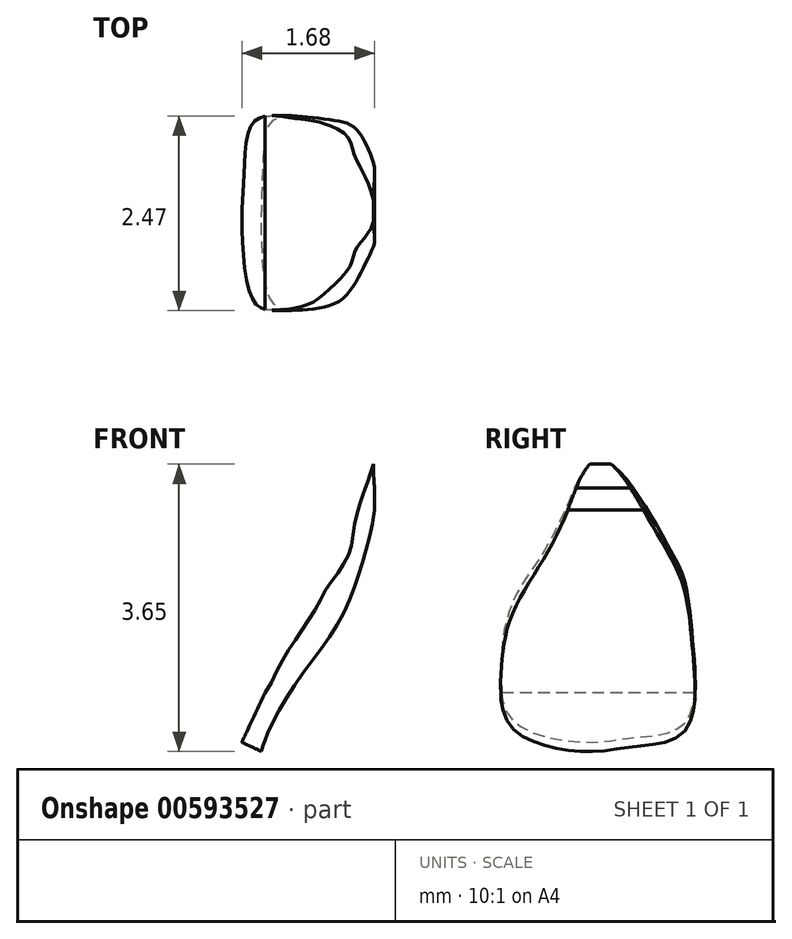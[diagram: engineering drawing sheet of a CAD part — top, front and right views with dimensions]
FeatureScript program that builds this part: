
annotation { "Feature Type Name" : "Feature", "Feature Type Description" : "" }
export const myFeature = defineFeature(function(context is Context, id is Id, definition is map)
    precondition{}
    {
        {
            var Q0;
            Q0=qCreatedBy(makeId("Right.planeOp"),FACE);
            var sketch = newSketch(context, id + "F0", { "sketchPlane" : qUnion([Q0])});
            skFitSpline(sketch, "E0", {"points": [v(-2.15, -4.24) * mm, v(-1.2, -4.53) * mm, v(-0.65, -4.46) * mm, v(0, -4.27) * mm, v(0.11, -3.1) * mm, v(0, -2.14) * mm, v(-0.34, -1.44) * mm, v(-1.07, -0.56) * mm, v(-1.5, -1.21) * mm, v(-1.8, -1.8) * mm, v(-2.2, -2.6) * mm, v(-2.32, -3.48) * mm, v(-2.15, -4.24) * mm]});
            skSolve(sketch);
        }
        {
            var Q0;
            Q0 = qSketchRegion(id + "F0", true);
            extrude(context, id + "F1", {"entities" : qUnion([Q0]), "endBound" : BoundingType.SYMMETRIC, "depth" : 0.6 * mm, "offsetDistance" : 25 * mm});
        }
        {
            var Q0;
            Q0=qCreatedBy(makeId("Right.planeOp"),FACE);
            var sketch = newSketch(context, id + "F2", { "sketchPlane" : qUnion([Q0])});
            skLineSegment(sketch, "E1", {"start": v(0, 11.64) * mm, "end": v(0, -10.45) * mm});
            skLineSegment(sketch, "E2", {"start": v(-11.55, 0) * mm, "end": v(15.23, 0) * mm});
            skSolve(sketch);
        }
        {
            var Q0;
            Q0=makeQuery(id+"F1.opExtrude","SWEPT_BODY",BODY,{"disambiguationData":[OSD([sQuery(id+"F0.wireOp",EDGE,"E0")])]});
            var Q1;
            Q1=sQuery(id+"F2.wireOp",EDGE,"E2");
            transform(context, id + "F3", {"entities" : qUnion([Q0]), "transformType" : TransformType.ROTATION, "transformAxis" : qUnion([Q1]), "angle" : 25 * degree, "makeCopy" : false});
        }
        {
            var Q0;
            Q0=makeQuery(id+"F1.opExtrude","SWEPT_BODY",BODY,{"disambiguationData":[OSD([sQuery(id+"F0.wireOp",EDGE,"E0")])]});
            transform(context, id + "F4", {"entities" : qUnion([Q0]), "transformType" : TransformType.TRANSLATION_3D, "dx" : 4.1 * mm, "dy" : 0 * mm, "dz" : 0 * mm, "makeCopy" : false});
        }
        {
            var Q0;
            Q0=makeQuery(id+"F1.opExtrude","CAP_FACE",FACE,{"disambiguationData":[OSD([sQuery(id+"F0.wireOp",EDGE,"E0")])],"isStart":false});
            var sketch = newSketch(context, id + "F5", { "sketchPlane" : qUnion([Q0])});
            skPoint(sketch, "E3", {"position": v(-2.32, -1.62) * mm});
            skSolve(sketch);
        }
        {
            var Q0;
            Q0=sQuery(id+"F5.wireOp",VERTEX,"E3");
            var Q1;
            Q1=qCreatedBy(makeId("Front.planeOp"),FACE);
            cPlane(context, id + "F6", {"entities" : qUnion([Q0, Q1]), "cplaneType" : CPlaneType.PLANE_POINT, "offset" : 25 * mm, "width" : 150 * mm, "height" : 150 * mm});
        }
        {
            var Q0;
            Q0=qCreatedBy(id+"F6.planeOp",FACE);
            var sketch = newSketch(context, id + "F7", { "sketchPlane" : qUnion([Q0])});
            skFitSpline(sketch, "E4", {"points": [v(2.2, -3.35) * mm, v(2.47, -2.85) * mm, v(2.82, -2.32) * mm, v(2.97, -2.03) * mm, v(3.25, -1.62) * mm, v(3.34, -1.17) * mm, v(3.6, -0.36) * mm, v(3.08, -1.36) * mm, v(2.99, -1.6) * mm, v(2.4, -2.72) * mm, v(2.2, -3.35) * mm]});
            skFitSpline(sketch, "E5", {"points": [v(2.16, -4.08) * mm, v(2.4, -3.52) * mm, v(2.75, -3) * mm, v(3.08, -2.54) * mm, v(3.31, -2.07) * mm, v(3.48, -1.53) * mm, v(3.6, -1.02) * mm, v(3.6, -0.74) * mm, v(3.6, -0.36) * mm, v(3.77, -1.3) * mm, v(2.68, -4.35) * mm, v(2.21, -4.34) * mm, v(2.16, -4.08) * mm]});
            skLineSegment(sketch, "E6", {"start": v(4.12, -1.75) * mm, "end": v(3.6, -1.35) * mm});
            skLineSegment(sketch, "E7", {"start": v(3.6, -1.35) * mm, "end": v(3.6, -0.27) * mm});
            skLineSegment(sketch, "E8", {"start": v(3.6, -0.27) * mm, "end": v(4.67, -0.88) * mm});
            skLineSegment(sketch, "E9", {"start": v(4.67, -0.88) * mm, "end": v(4.12, -1.75) * mm});
            skSolve(sketch);
        }
        {
            var Q0;
            Q0 = qSketchRegion(id + "F7", true);
            extrude(context, id + "F8", {"entities" : qUnion([Q0]), "operationType" : NewBodyOperationType.REMOVE, "endBound" : BoundingType.SYMMETRIC, "oppositeDirection" : true, "depth" : 5 * mm, "offsetDistance" : 25 * mm});
        }
    });
